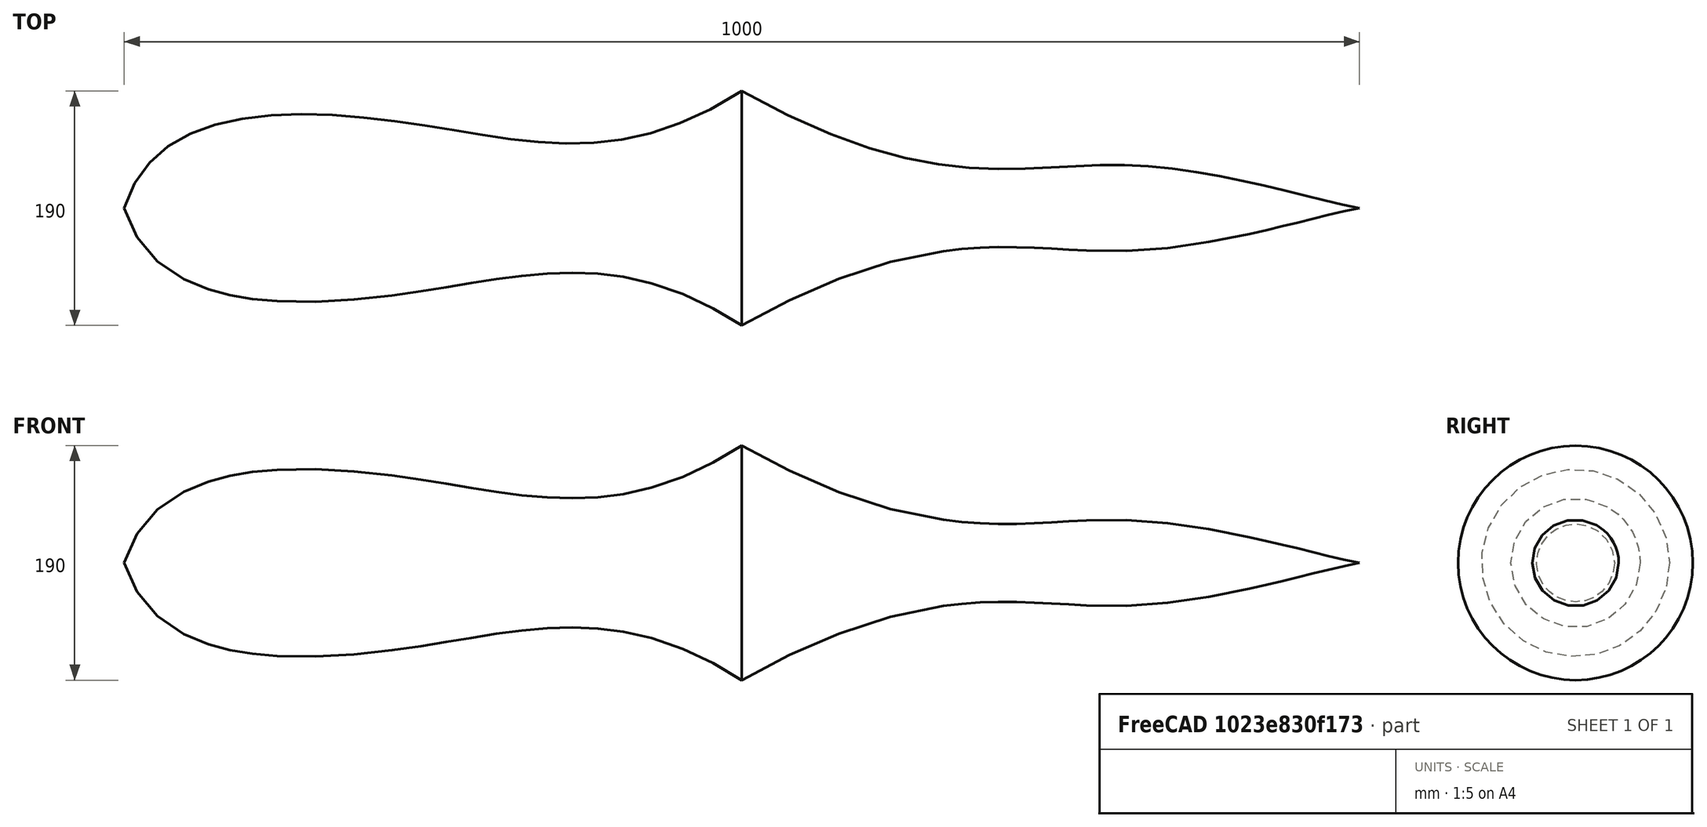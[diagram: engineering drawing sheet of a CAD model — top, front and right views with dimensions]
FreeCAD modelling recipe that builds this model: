
FCSTD DOCUMENT  (FreeCAD 0.20R29177 +426 (Git))
Label: UUV_hull_optimization
License: All rights reserved
LicenseURL: http://en.wikipedia.org/wiki/All_rights_reserved
objects: Sketcher::SketchObject×1, PartDesign::Revolution×1, PartDesign::Body×1, TechDraw::DrawSVGTemplate×1, TechDraw::DrawViewPart×1, TechDraw::DrawViewSection×1, TechDraw::DrawPage×1, Spreadsheet::Sheet×1
note: 4 computed .brp shape members not serialized (recipe doc carries the construction recipe); baked Part::Feature solids carry a one-line shape summary decoded from their .brp

FEATURE [Sketcher::SketchObject] Sketch
  FullyConstrained = true
  MapMode = 5
  Support = -> [XY_Plane]
  expr: .Constraints.fifth_y = <<Spreadsheet>>.B6
  expr: .Constraints.first_y = <<Spreadsheet>>.B2
  expr: .Constraints.fourth_y = <<Spreadsheet>>.B5
  expr: .Constraints.nose = <<Spreadsheet>>.B1
  expr: .Constraints.part_b = 1000mm - .Constraints.nose
  expr: .Constraints.second_y = <<Spreadsheet>>.B3
  expr: .Constraints.sixth_y = <<Spreadsheet>>.B7
  expr: .Constraints.third_y = <<Spreadsheet>>.B4
  expr: Constraints[43] = .Constraints.nose * 0.05
  expr: Constraints[44] = .Constraints.nose * 0.5
  expr: Constraints[45] = .Constraints.nose * 0.8
  expr: Constraints[46] = .Constraints.part_b * 0.3
  expr: Constraints[47] = .Constraints.part_b * 0.6
  expr: Constraints[48] = .Constraints.part_b * 0.9
  sketch-geometry (19):
    g0: LineSegment StartX=-250 StartY=95 StartZ=0 EndX=-250 EndY=0 EndZ=0
    g1: LineSegment StartX=-250 StartY=0 StartZ=0 EndX=250 EndY=0 EndZ=0
    g2: LineSegment StartX=-250 StartY=0 StartZ=0 EndX=-750 EndY=0 EndZ=0
    g3-g7: Circle x5 (B-spline internal-alignment scaffolding for g8; pole/knot coordinates omitted)
    g8: BSplineCurve PolesCount=5 KnotsCount=3 Degree=3 IsPeriodic=0
    g9: GeomPoint X=-750 Y=0 Z=0
    g10: GeomPoint X=-250 Y=95 Z=0
    g11-g15: Circle x5 (B-spline internal-alignment scaffolding for g16; pole/knot coordinates omitted)
    g16: BSplineCurve PolesCount=5 KnotsCount=3 Degree=3 IsPeriodic=0
    g17: GeomPoint X=-250 Y=95 Z=0
    g18: GeomPoint X=250 Y=0 Z=0
  constraints (35):
    c: Vertical(g0)
    c: Symmetric(g0,g1,g-2)
    c: Coincident(g1,g0)
    c: Coincident(g2,g0)
    c: PointOnObject(g2,g-1)
    c: Horizontal(g2)
    c: Coincident(g8,g2)
    c: Weight(g3) = 1
    c: Equal(g3, g4-g7) x4
    c: Coincident(g8,g0)
    c: InternalAlignment(g3-g7 -> g8) x5
    c: InternalAlignment(g9,g8)
    c: InternalAlignment(g10,g8)
    c: Coincident(g16,g8)
    c: Weight(g11) = 1
    c: Equal(g11, g12-g15) x4
    c: Coincident(g16,g1)
    c: InternalAlignment(g11-g15 -> g16) x5
    c: InternalAlignment(g17,g16)
    c: InternalAlignment(g18,g16)
    c: DistanceX(g2,g1) = 500  'nose'
    c: DistanceX(g1,g1) = 500  'part_b'
    c: DistanceY(g1,g8) = 95  'radius'
    c: DistanceY(g2,g4) = 85  'first_y'
    c: DistanceY(g2,g5) = 80  'second_y'
    c: DistanceY(g2,g6) = 30  'third_y'
    c: DistanceY(g2,g12) = 10  'fourth_y'
    c: DistanceY(g2,g13) = 60  'fifth_y'
    c: DistanceY(g2,g14) = 10  'sixth_y'
    c: DistanceX(g2,g4) = 25
    c: DistanceX(g2,g5) = 250
    c: DistanceX(g2,g6) = 400
    c: DistanceX(g1,g12) = 150
    c: DistanceX(g1,g13) = 300
    c: DistanceX(g1,g14) = 450
FEATURE [PartDesign::Revolution] Revolution
  Angle = 360
  Axis = (1,0,0)
  Base = (0,0,0)
  Profile = -> Sketch
  ReferenceAxis = -> Sketch [H_Axis]
FEATURE [PartDesign::Body] Body
  Group = -> [Sketch,Revolution]
  Origin = -> Origin
  Tip = -> Revolution
FEATURE [TechDraw::DrawSVGTemplate] Template
  EditableTexts = Designed_by_Name=Designed by Name; Drawing_number=Drawing number; FC-Date=Date; FC-SC=Scale; FC-SH=Sheet; FC-Title=Title; Subtitle=Subtitle; Weight=Weight
  Height = 210
  Orientation = 1
  Width = 297
FEATURE [TechDraw::DrawViewPart] View
  CoarseView = false
  Direction = (0,0,1)
  Focus = 100
  HardHidden = false
  IsoCount = 0
  IsoHidden = false
  IsoVisible = false
  LockPosition = false
  Perspective = false
  Rotation = 0
  Scale = 0.05
  ScaleType = 2
  SeamHidden = false
  SeamVisible = true
  SmoothHidden = false
  SmoothVisible = true
  Source = -> [Body]
  X = 65.7614
  XDirection = (1,0,0)
  Y = 42.7117
FEATURE [TechDraw::DrawViewSection] SectionView  label="Section  - "
  BaseView = -> View
  CoarseView = false
  CutSurfaceDisplay = 2
  Direction = (0,1,0)
  FileGeomPattern = <path>
  FileHatchPattern = <path>
  Focus = 100
  FuseBeforeCut = false
  HardHidden = false
  HatchScale = 1
  IsoCount = 0
  IsoHidden = false
  IsoVisible = false
  LockPosition = false
  NameGeomPattern = Diamond
  Perspective = false
  Rotation = 0
  Scale = 0.1
  ScaleType = 2
  SeamHidden = false
  SeamVisible = true
  SectionDirection = 3
  SectionNormal = (0,1,0)
  SectionOrigin = (0,0,0)
  SmoothHidden = false
  SmoothVisible = true
  Source = -> [Body]
  X = 144.754
  XDirection = (1,0,0)
  Y = 127.102
FEATURE [TechDraw::DrawPage] Page
  KeepUpdated = true
  NextBalloonIndex = 1
  ProjectionType = 0
  Template = -> Template
  Views = -> [View,SectionView]
FEATURE [Spreadsheet::Sheet] Spreadsheet
  cells = A1=nose; B1==500mm; A2=first_y; B2==85mm; A3=second_y; B3==80mm; A4=third_y; B4==30mm; A5=fourth_y; B5==10mm; A6=fifth_y; B6==60mm; A7=sixth_y; B7==10mm
note: 2 file-system paths scrubbed to <path> (originals preserved in the JSON sidecar)
